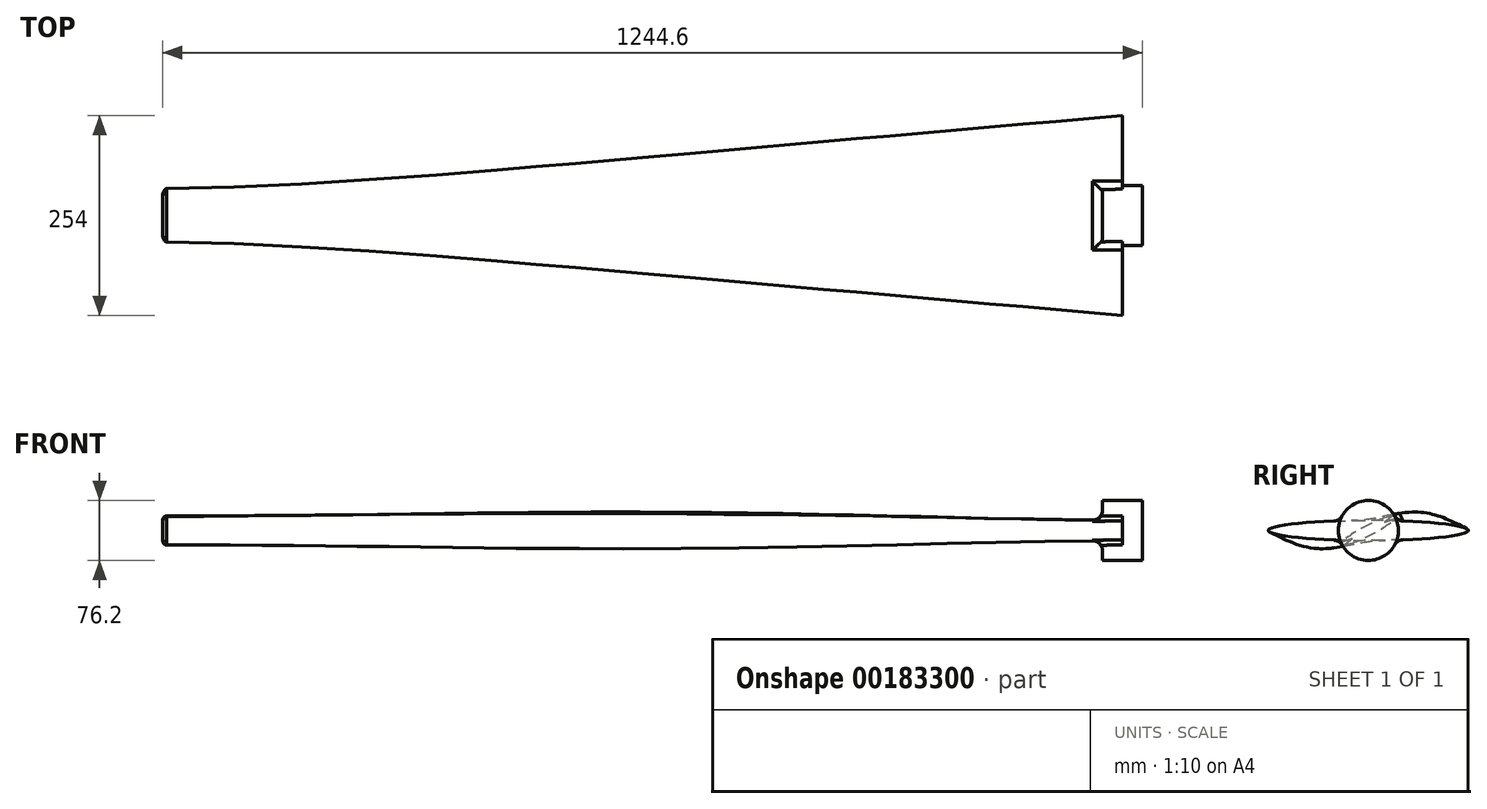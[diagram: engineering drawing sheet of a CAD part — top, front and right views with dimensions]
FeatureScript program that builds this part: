
annotation { "Feature Type Name" : "Feature", "Feature Type Description" : "" }
export const myFeature = defineFeature(function(context is Context, id is Id, definition is map)
    precondition{}
    {
        {
            var Q0;
            Q0=qCreatedBy(makeId("Right.planeOp"),FACE);
            cPlane(context, id + "F0", {"entities" : qUnion([Q0]), "cplaneType" : CPlaneType.OFFSET, "offset" : 1219.2 * mm, "oppositeDirection" : true, "width" : 152.4 * mm, "height" : 152.4 * mm});
        }
        {
            var Q0;
            Q0=qCreatedBy(makeId("Right.planeOp"),FACE);
            cPlane(context, id + "F1", {"entities" : qUnion([Q0]), "cplaneType" : CPlaneType.OFFSET, "offset" : 609.6 * mm, "oppositeDirection" : true, "width" : 152.4 * mm, "height" : 152.4 * mm});
        }
        {
            var Q0;
            Q0=qCreatedBy(id+"F0.planeOp",FACE);
            var sketch = newSketch(context, id + "F2", { "sketchPlane" : qUnion([Q0])});
            skEllipse(sketch, "E0", {"center": v(0, 0) * mm, "majorRadius": 38.1 * mm, "minorRadius": 6.35 * mm, "majorAxis": v(0.89, 0.46)});
            skSolve(sketch);
        }
        {
            var Q0;
            Q0=qCreatedBy(id+"F1.planeOp",FACE);
            var sketch = newSketch(context, id + "F3", { "sketchPlane" : qUnion([Q0])});
            skEllipse(sketch, "E1", {"center": v(0, 0) * mm, "majorRadius": 76.2 * mm, "minorRadius": 12.7 * mm, "majorAxis": v(0.97, 0.26)});
            skSolve(sketch);
        }
        {
            var Q0;
            Q0=qCreatedBy(makeId("Right.planeOp"),FACE);
            var sketch = newSketch(context, id + "F4", { "sketchPlane" : qUnion([Q0])});
            skEllipse(sketch, "E2", {"center": v(0, 0) * mm, "majorRadius": 127 * mm, "minorRadius": 12.7 * mm, "majorAxis": v(1, 0)});
            skLineSegment(sketch, "E3", {"start": v(0, 0) * mm, "end": v(0, 254) * mm, "construction": true});
            skSolve(sketch);
        }
        {
            var Q0;
            Q0=makeQuery(id+"F2.imprint","IMPRINT",FACE,{"disambiguationData":[TD([[makeQuery(id+"F2.imprint","IMPRINT",EDGE,{"derivedFrom":sQuery(id+"F2.wireOp",EDGE,"E0")}),1.0]])]});
            var Q1;
            Q1=makeQuery(id+"F3.imprint","IMPRINT",FACE,{"disambiguationData":[TD([[makeQuery(id+"F3.imprint","IMPRINT",EDGE,{"derivedFrom":sQuery(id+"F3.wireOp",EDGE,"E1")}),1.0]])]});
            var Q2;
            Q2=makeQuery(id+"F4.imprint","IMPRINT",FACE,{"disambiguationData":[TD([[makeQuery(id+"F4.imprint","IMPRINT",EDGE,{"derivedFrom":sQuery(id+"F4.wireOp",EDGE,"E2")}),1.0]])]});
            loft(context, id + "F5", {"sheetProfilesArray" : [{ "sheetProfileEntities" : qUnion([Q0]) }, { "sheetProfileEntities" : qUnion([Q1]) }, { "sheetProfileEntities" : qUnion([Q2]) }]});
        }
        {
            var Q0;
            Q0=makeQuery(id+"F5.opLoft","MID_CAP_EDGE",EDGE,{"disambiguationData":[OSD([sQuery(id+"F2.wireOp",EDGE,"E0")])],"capPos":0.0});
            fillet(context, id + "F6", {"entities" : qUnion([Q0]), "radius" : 5.08 * mm, "tangentPropagation" : true, "allowEdgeOverflow" : false});
        }
        {
            var Q0;
            Q0=qCreatedBy(makeId("Right.planeOp"),FACE);
            var sketch = newSketch(context, id + "F7", { "sketchPlane" : qUnion([Q0])});
            skCircle(sketch, "E4", {"center": v(0, 0) * mm, "radius": 38.1 * mm});
            skSolve(sketch);
        }
        {
            var Q0;
            Q0=makeQuery(id+"F7.imprint","IMPRINT",FACE,{"disambiguationData":[TD([[makeQuery(id+"F7.imprint","IMPRINT",EDGE,{"derivedFrom":sQuery(id+"F7.wireOp",EDGE,"E4")}),1.0]])]});
            extrude(context, id + "F8", {"entities" : qUnion([Q0]), "operationType" : NewBodyOperationType.ADD, "endBound" : BoundingType.SYMMETRIC, "depth" : 50.8 * mm});
        }
        {
            var Q0;
            Q0=makeQuery(id+"F8.boolean.opBoolean","INTERSECT",EDGE,{"disambiguationData":[OD(1.0)],"derivedFrom":[makeQuery(id+"F5.opLoft","SWEPT_FACE",FACE,{"disambiguationData":[OSD([sQuery(id+"F2.wireOp",EDGE,"E0"),sQuery(id+"F3.wireOp",EDGE,"E1")])]}),makeQuery(id+"F8.opExtrude","CAP_FACE",FACE,{"disambiguationData":[OSD([sQuery(id+"F7.wireOp",EDGE,"E4")])],"isStart":true})]});
            var Q1;
            Q1=makeQuery(id+"F8.boolean.opBoolean","INTERSECT",EDGE,{"disambiguationData":[OD(1.0)],"derivedFrom":[makeQuery(id+"F5.opLoft","SWEPT_FACE",FACE,{"disambiguationData":[OSD([sQuery(id+"F2.wireOp",EDGE,"E0"),sQuery(id+"F3.wireOp",EDGE,"E1")])]}),makeQuery(id+"F8.opExtrude","SWEPT_FACE",FACE,{"disambiguationData":[OSD([sQuery(id+"F7.wireOp",EDGE,"E4")])]})]});
            var Q2;
            Q2=makeQuery(id+"F8.boolean.opBoolean","INTERSECT",EDGE,{"disambiguationData":[OD(3.0)],"derivedFrom":[makeQuery(id+"F5.opLoft","SWEPT_FACE",FACE,{"disambiguationData":[OSD([sQuery(id+"F2.wireOp",EDGE,"E0"),sQuery(id+"F3.wireOp",EDGE,"E1")])]}),makeQuery(id+"F8.opExtrude","SWEPT_FACE",FACE,{"disambiguationData":[OSD([sQuery(id+"F7.wireOp",EDGE,"E4")])]})]});
            fillet(context, id + "F9", {"entities" : qUnion([Q0, Q1, Q2]), "radius" : 12.7 * mm, "tangentPropagation" : true, "allowEdgeOverflow" : false});
        }
        {
            var Q0;
            Q0=makeQuery(id+"F8.boolean.opBoolean","INTERSECT",EDGE,{"disambiguationData":[OD(2.0)],"derivedFrom":[makeQuery(id+"F5.opLoft","SWEPT_FACE",FACE,{"disambiguationData":[OSD([sQuery(id+"F2.wireOp",EDGE,"E0"),sQuery(id+"F3.wireOp",EDGE,"E1")])]}),makeQuery(id+"F8.opExtrude","SWEPT_FACE",FACE,{"disambiguationData":[OSD([sQuery(id+"F7.wireOp",EDGE,"E4")])]})]});
            var Q1;
            Q1=makeQuery(id+"F8.boolean.opBoolean","INTERSECT",EDGE,{"disambiguationData":[OD(0.0)],"derivedFrom":[makeQuery(id+"F5.opLoft","SWEPT_FACE",FACE,{"disambiguationData":[OSD([sQuery(id+"F2.wireOp",EDGE,"E0"),sQuery(id+"F3.wireOp",EDGE,"E1")])]}),makeQuery(id+"F8.opExtrude","CAP_FACE",FACE,{"disambiguationData":[OSD([sQuery(id+"F7.wireOp",EDGE,"E4")])],"isStart":true})]});
            var Q2;
            Q2=makeQuery(id+"F8.boolean.opBoolean","INTERSECT",EDGE,{"disambiguationData":[OD(0.0)],"derivedFrom":[makeQuery(id+"F5.opLoft","SWEPT_FACE",FACE,{"disambiguationData":[OSD([sQuery(id+"F2.wireOp",EDGE,"E0"),sQuery(id+"F3.wireOp",EDGE,"E1")])]}),makeQuery(id+"F8.opExtrude","SWEPT_FACE",FACE,{"disambiguationData":[OSD([sQuery(id+"F7.wireOp",EDGE,"E4")])]})]});
            fillet(context, id + "F10", {"entities" : qUnion([Q0, Q1, Q2]), "radius" : 12.7 * mm, "tangentPropagation" : true, "allowEdgeOverflow" : false});
        }
    });
